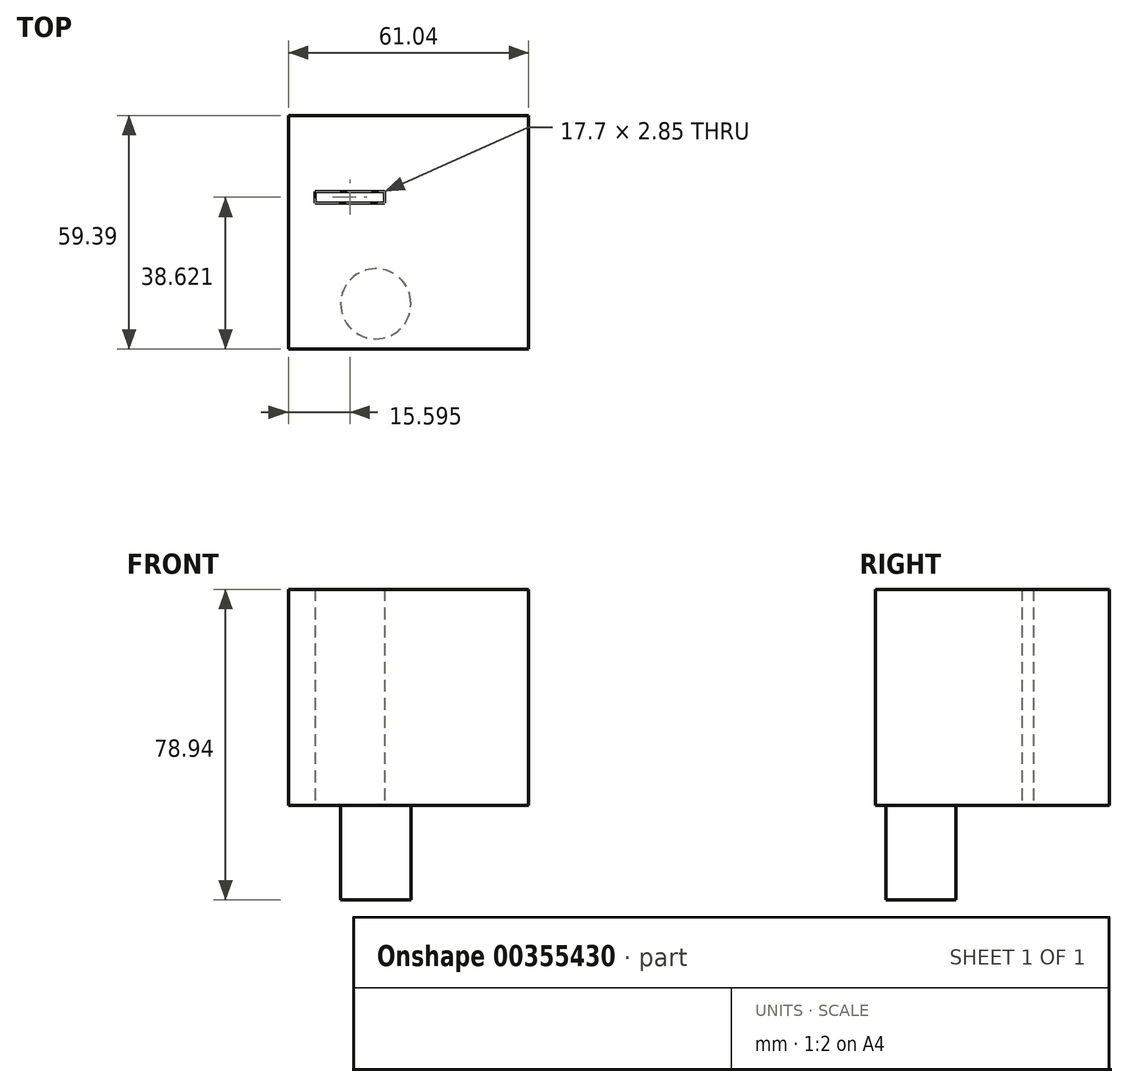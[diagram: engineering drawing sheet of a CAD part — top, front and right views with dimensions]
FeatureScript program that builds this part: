
annotation { "Feature Type Name" : "Feature", "Feature Type Description" : "" }
export const myFeature = defineFeature(function(context is Context, id is Id, definition is map)
    precondition{}
    {
        {
            var Q0;
            Q0=qCreatedBy(makeId("Top.planeOp"),FACE);
            var sketch = newSketch(context, id + "F0", { "sketchPlane" : qUnion([Q0])});
            skLineSegment(sketch, "E0.bottom", {"start": v(-45.74, 28.5) * mm, "end": v(-28.05, 28.5) * mm});
            skLineSegment(sketch, "E0.top", {"start": v(-45.74, 25.65) * mm, "end": v(-28.05, 25.65) * mm});
            skLineSegment(sketch, "E0.left", {"start": v(-45.74, 28.5) * mm, "end": v(-45.74, 25.65) * mm});
            skLineSegment(sketch, "E0.right", {"start": v(-28.05, 28.5) * mm, "end": v(-28.05, 25.65) * mm});
            skLineSegment(sketch, "E1.bottom", {"start": v(8.55, -11.55) * mm, "end": v(-52.5, -11.55) * mm});
            skLineSegment(sketch, "E1.top", {"start": v(8.55, 47.84) * mm, "end": v(-52.5, 47.84) * mm});
            skLineSegment(sketch, "E1.left", {"start": v(8.55, -11.55) * mm, "end": v(8.55, 47.84) * mm});
            skLineSegment(sketch, "E1.right", {"start": v(-52.5, -11.55) * mm, "end": v(-52.5, 47.84) * mm});
            skSolve(sketch);
        }
        {
            var Q0;
            Q0 = qSketchRegion(id + "F0", true);
            extrude(context, id + "F1", {"entities" : qUnion([Q0]), "depth" : 54.9 * mm});
        }
        {
            var Q0;
            Q0=qCreatedBy(makeId("Top.planeOp"),FACE);
            var sketch = newSketch(context, id + "F2", { "sketchPlane" : qUnion([Q0])});
            skCircle(sketch, "E2", {"center": v(-30.3, 0) * mm, "radius": 8.92 * mm});
            skSolve(sketch);
        }
        {
            var Q0;
            Q0 = qSketchRegion(id + "F2", true);
            extrude(context, id + "F3", {"entities" : qUnion([Q0]), "operationType" : NewBodyOperationType.ADD, "oppositeDirection" : true, "depth" : 24.04 * mm});
        }
    });
